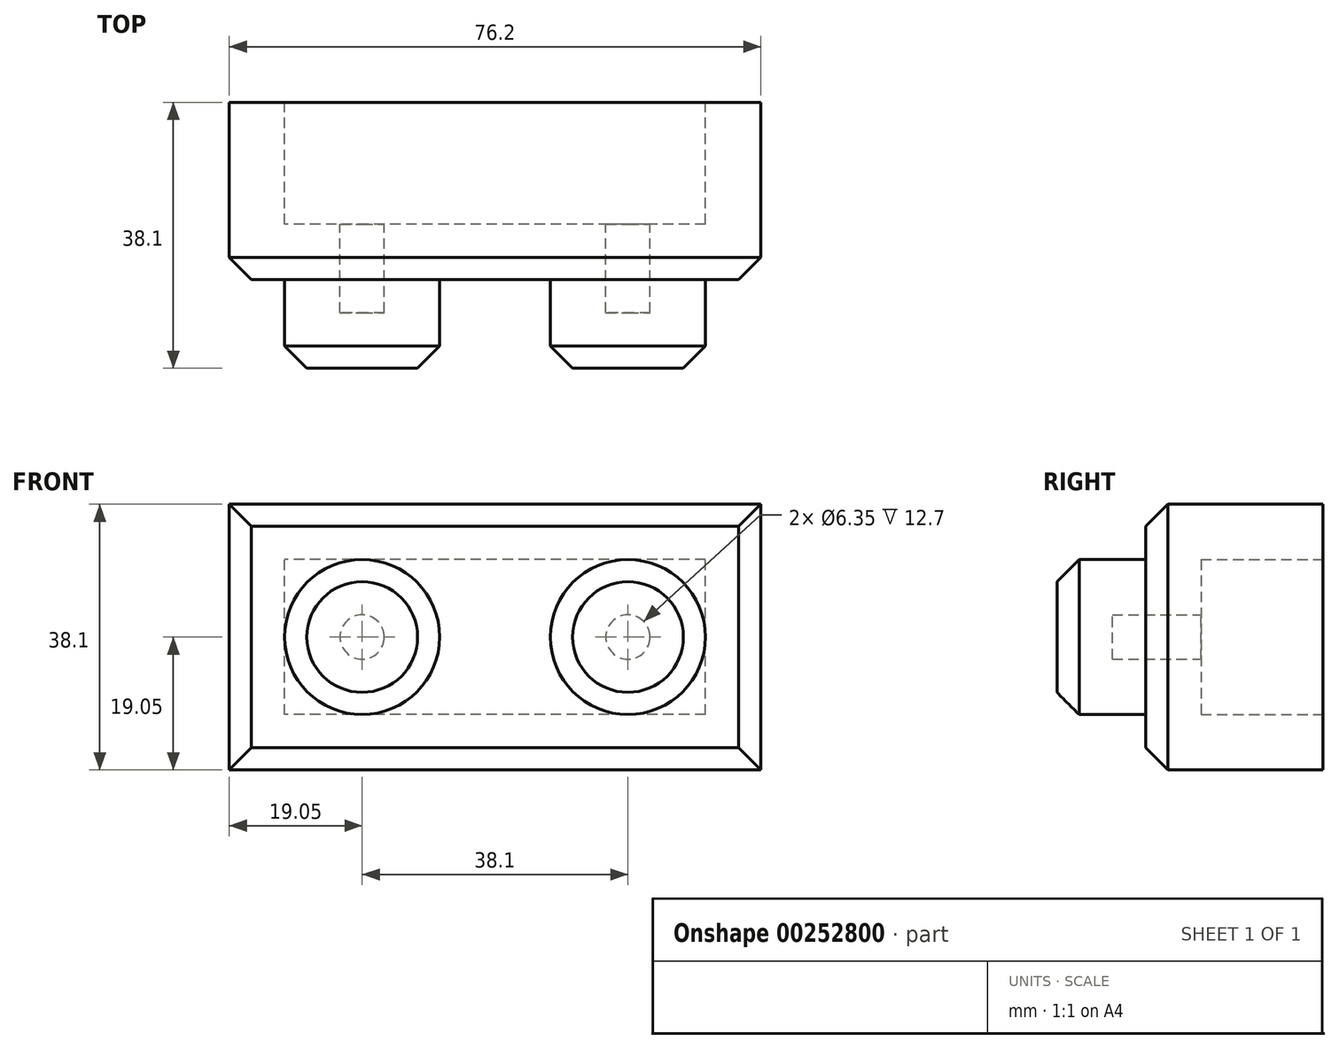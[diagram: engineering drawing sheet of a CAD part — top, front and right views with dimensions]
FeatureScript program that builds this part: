
annotation { "Feature Type Name" : "Feature", "Feature Type Description" : "" }
export const myFeature = defineFeature(function(context is Context, id is Id, definition is map)
    precondition{}
    {
        {
            var Q0;
            Q0=qCreatedBy(makeId("Front.planeOp"),FACE);
            var sketch = newSketch(context, id + "F0", { "sketchPlane" : qUnion([Q0])});
            skLineSegment(sketch, "E0.bottom", {"start": v(38.1, -19.05) * mm, "end": v(-38.1, -19.05) * mm});
            skLineSegment(sketch, "E0.top", {"start": v(38.1, 19.05) * mm, "end": v(-38.1, 19.05) * mm});
            skLineSegment(sketch, "E0.left", {"start": v(38.1, -19.05) * mm, "end": v(38.1, 19.05) * mm});
            skLineSegment(sketch, "E0.right", {"start": v(-38.1, -19.05) * mm, "end": v(-38.1, 19.05) * mm});
            skPoint(sketch, "E0.middle", {"position": v(0, 0) * mm});
            skSolve(sketch);
        }
        {
            var Q0;
            Q0 = qSketchRegion(id + "F0", true);
            extrude(context, id + "F1", {"entities" : qUnion([Q0]), "depth" : 25.4 * mm});
        }
        {
            var Q0;
            Q0=makeQuery(id+"F1.opExtrude","CAP_FACE",FACE,{"disambiguationData":[OSD([sQuery(id+"F0.wireOp",EDGE,"E0.bottom"),sQuery(id+"F0.wireOp",EDGE,"E0.top"),sQuery(id+"F0.wireOp",EDGE,"E0.left"),sQuery(id+"F0.wireOp",EDGE,"E0.right")])],"isStart":false});
            var sketch = newSketch(context, id + "F2", { "sketchPlane" : qUnion([Q0])});
            skCircle(sketch, "E1", {"center": v(-19.05, 0) * mm, "radius": 11.11 * mm});
            skCircle(sketch, "E2", {"center": v(19.05, 0) * mm, "radius": 11.11 * mm});
            skSolve(sketch);
        }
        {
            var Q0;
            Q0 = qSketchRegion(id + "F2", true);
            extrude(context, id + "F3", {"entities" : qUnion([Q0]), "operationType" : NewBodyOperationType.ADD, "depth" : 12.7 * mm});
        }
        {
            var Q0;
            Q0=makeQuery(id+"F3.opExtrude","CAP_EDGE",EDGE,{"disambiguationData":[OSD([sQuery(id+"F2.wireOp",EDGE,"E2")])],"isStart":false});
            var Q1;
            Q1=makeQuery(id+"F3.opExtrude","CAP_EDGE",EDGE,{"disambiguationData":[OSD([sQuery(id+"F2.wireOp",EDGE,"E1")])],"isStart":false});
            chamfer(context, id + "F4", {"entities" : qUnion([Q0, Q1]), "chamferType" : ChamferType.OFFSET_ANGLE, "width" : 3.17 * mm, "oppositeDirection" : false, "angle" : 45 * degree, "tangentPropagation" : true});
        }
        {
            var Q0;
            Q0=makeQuery(id+"F1.opExtrude","CAP_EDGE",EDGE,{"disambiguationData":[OSD([sQuery(id+"F0.wireOp",EDGE,"E0.top")])],"isStart":false});
            chamfer(context, id + "F5", {"entities" : qUnion([Q0]), "chamferType" : ChamferType.OFFSET_ANGLE, "width" : 3.17 * mm, "oppositeDirection" : false, "angle" : 45 * degree, "tangentPropagation" : true});
        }
        {
            var Q0;
            Q0=makeQuery(id+"F1.opExtrude","CAP_EDGE",EDGE,{"disambiguationData":[OSD([sQuery(id+"F0.wireOp",EDGE,"E0.left")])],"isStart":false});
            var Q1;
            Q1=makeQuery(id+"F1.opExtrude","CAP_EDGE",EDGE,{"disambiguationData":[OSD([sQuery(id+"F0.wireOp",EDGE,"E0.bottom")])],"isStart":false});
            var Q2;
            Q2=makeQuery(id+"F1.opExtrude","CAP_EDGE",EDGE,{"disambiguationData":[OSD([sQuery(id+"F0.wireOp",EDGE,"E0.right")])],"isStart":false});
            chamfer(context, id + "F6", {"entities" : qUnion([Q0, Q1, Q2]), "chamferType" : ChamferType.OFFSET_ANGLE, "width" : 3.17 * mm, "oppositeDirection" : false, "angle" : 45 * degree, "tangentPropagation" : true});
        }
        {
            var Q0;
            Q0=makeQuery(id+"F1.opExtrude","CAP_FACE",FACE,{"disambiguationData":[OSD([sQuery(id+"F0.wireOp",EDGE,"E0.bottom"),sQuery(id+"F0.wireOp",EDGE,"E0.top"),sQuery(id+"F0.wireOp",EDGE,"E0.left"),sQuery(id+"F0.wireOp",EDGE,"E0.right")])],"isStart":true});
            shell(context, id + "F7", {"entities" : qUnion([Q0]), "thickness" : 7.94 * mm});
        }
    });
